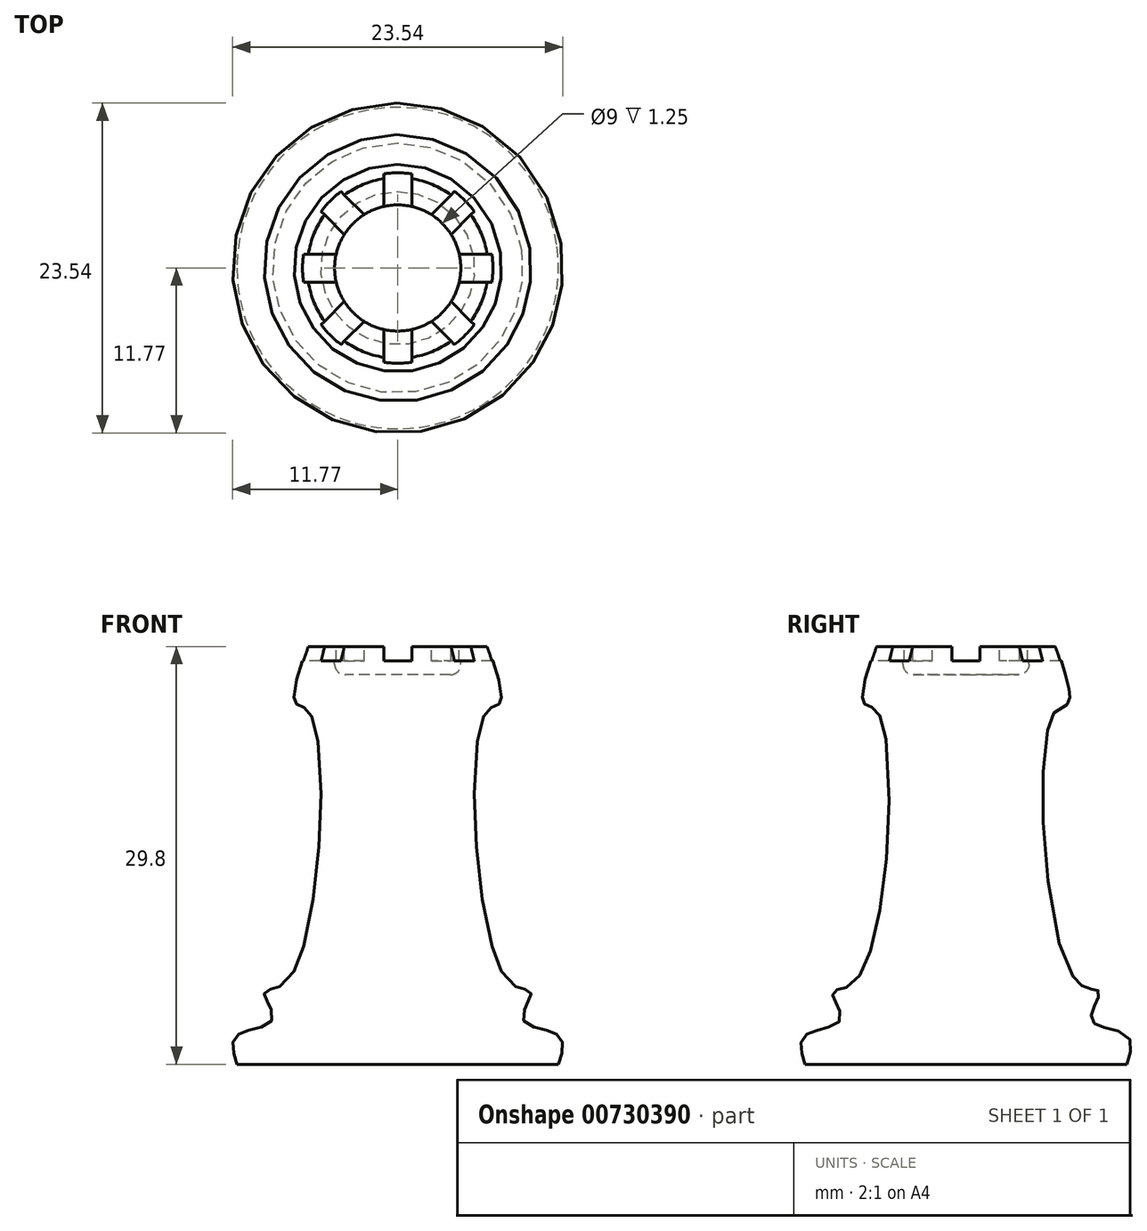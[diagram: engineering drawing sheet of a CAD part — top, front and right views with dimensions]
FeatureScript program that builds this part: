
annotation { "Feature Type Name" : "Feature", "Feature Type Description" : "" }
export const myFeature = defineFeature(function(context is Context, id is Id, definition is map)
    precondition{}
    {
        {
            var Q0;
            Q0=qCreatedBy(makeId("Front.planeOp"),FACE);
            var sketch = newSketch(context, id + "F0", { "sketchPlane" : qUnion([Q0])});
            skLineSegment(sketch, "E0", {"start": v(0, 0) * mm, "end": v(0, 29.8) * mm});
            skLineSegment(sketch, "E1", {"start": v(0, 0) * mm, "end": v(11.47, 0) * mm});
            skFitSpline(sketch, "E2", {"points": [v(11.47, 0) * mm, v(11.47, 2.06) * mm, v(8.96, 3.18) * mm, v(9.52, 5.13) * mm, v(7.84, 5.97) * mm, v(6.17, 24.93) * mm, v(7.29, 25.77) * mm, v(6.45, 29.8) * mm], "startDerivative": vector(7.38, 22.92) * mm, "endDerivative": vector(-11.94, 34.46) * mm});
            skLineSegment(sketch, "E3", {"start": v(6.45, 29.8) * mm, "end": v(0, 29.8) * mm});
            skSolve(sketch);
        }
        {
            var Q0;
            Q0=makeQuery(id+"F0.imprint","IMPRINT",FACE,{"disambiguationData":[TD([[makeQuery(id+"F0.imprint","IMPRINT",EDGE,{"derivedFrom":sQuery(id+"F0.wireOp",EDGE,"E0")}),-1.0]])]});
            var Q1;
            Q1=sQuery(id+"F0.wireOp",EDGE,"E0");
            revolve(context, id + "F1", {"surfaceOperationType" : NewSurfaceOperationType.NEW, "entities" : qUnion([Q0]), "axis" : qUnion([Q1]), "revolveType" : RevolveType.FULL});
        }
        {
            var Q0;
            Q0=makeQuery(id+"F1.opRevolve","SWEPT_FACE",FACE,{"disambiguationData":[OSD([sQuery(id+"F0.wireOp",EDGE,"E3")])]});
            var sketch = newSketch(context, id + "F2", { "sketchPlane" : qUnion([Q0])});
            skCircle(sketch, "E4", {"center": v(0, 0) * mm, "radius": 4.5 * mm});
            skSolve(sketch);
        }
        {
            var Q0;
            Q0=makeQuery(id+"F2.imprint","IMPRINT",FACE,{"disambiguationData":[TD([[makeQuery(id+"F2.imprint","IMPRINT",EDGE,{"derivedFrom":sQuery(id+"F2.wireOp",EDGE,"E4")}),1.0]])]});
            extrude(context, id + "F3", {"entities" : qUnion([Q0]), "operationType" : NewBodyOperationType.REMOVE, "oppositeDirection" : true, "depth" : 2 * mm, "offsetDistance" : 25 * mm});
        }
        {
            var Q0;
            Q0=makeQuery(id+"F1.opRevolve","SWEPT_FACE",FACE,{"disambiguationData":[OSD([sQuery(id+"F0.wireOp",EDGE,"E3")])]});
            var sketch = newSketch(context, id + "F4", { "sketchPlane" : qUnion([Q0])});
            skLineSegment(sketch, "E5.bottom", {"start": v(-1, 7.5) * mm, "end": v(1, 7.5) * mm});
            skLineSegment(sketch, "E5.top", {"start": v(-1, -7.5) * mm, "end": v(1, -7.5) * mm});
            skLineSegment(sketch, "E5.left", {"start": v(-1, 7.5) * mm, "end": v(-1, -7.5) * mm});
            skLineSegment(sketch, "E5.right", {"start": v(1, 7.5) * mm, "end": v(1, -7.5) * mm});
            skPoint(sketch, "E5.middle", {"position": v(0, 0) * mm});
            skLineSegment(sketch, "E6.1.0", {"start": v(6.01, 4.6) * mm, "end": v(-4.6, -6.01) * mm});
            skLineSegment(sketch, "E6.1.1", {"start": v(4.6, 6.01) * mm, "end": v(-6.01, -4.6) * mm});
            skLineSegment(sketch, "E6.1.2", {"start": v(4.6, 6.01) * mm, "end": v(6.01, 4.6) * mm});
            skLineSegment(sketch, "E6.1.3", {"start": v(-6.01, -4.6) * mm, "end": v(-4.6, -6.01) * mm});
            skLineSegment(sketch, "E6.2.0", {"start": v(7.5, -1) * mm, "end": v(-7.5, -1) * mm});
            skLineSegment(sketch, "E6.2.1", {"start": v(7.5, 1) * mm, "end": v(-7.5, 1) * mm});
            skLineSegment(sketch, "E6.2.2", {"start": v(7.5, 1) * mm, "end": v(7.5, -1) * mm});
            skLineSegment(sketch, "E6.2.3", {"start": v(-7.5, 1) * mm, "end": v(-7.5, -1) * mm});
            skLineSegment(sketch, "E6.3.0", {"start": v(4.6, -6.01) * mm, "end": v(-6.01, 4.6) * mm});
            skLineSegment(sketch, "E6.3.1", {"start": v(6.01, -4.6) * mm, "end": v(-4.6, 6.01) * mm});
            skLineSegment(sketch, "E6.3.2", {"start": v(6.01, -4.6) * mm, "end": v(4.6, -6.01) * mm});
            skLineSegment(sketch, "E6.3.3", {"start": v(-4.6, 6.01) * mm, "end": v(-6.01, 4.6) * mm});
            skLineSegment(sketch, "E6.4.0", {"start": v(-1, -7.5) * mm, "end": v(-1, 7.5) * mm});
            skLineSegment(sketch, "E6.4.1", {"start": v(1, -7.5) * mm, "end": v(1, 7.5) * mm});
            skLineSegment(sketch, "E6.4.2", {"start": v(1, -7.5) * mm, "end": v(-1, -7.5) * mm});
            skLineSegment(sketch, "E6.4.3", {"start": v(1, 7.5) * mm, "end": v(-1, 7.5) * mm});
            skLineSegment(sketch, "E6.anchor1", {"start": v(0, 0) * mm, "end": v(1, -7.5) * mm, "construction": true});
            skLineSegment(sketch, "E6.anchor2", {"start": v(0, 0) * mm, "end": v(-1, 7.5) * mm, "construction": true});
            skSolve(sketch);
        }
        {
            var Q0;
            Q0 = qSketchRegion(id + "F4", true);
            extrude(context, id + "F5", {"entities" : qUnion([Q0]), "operationType" : NewBodyOperationType.REMOVE, "oppositeDirection" : true, "depth" : 1 * mm, "offsetDistance" : 25 * mm});
        }
        {
            var Q0;
            Q0=makeQuery(id+"F3.boolean.opBoolean","COPY",EDGE,{"derivedFrom":makeQuery(id+"F3.opExtrude","CAP_EDGE",EDGE,{"disambiguationData":[OSD([sQuery(id+"F2.wireOp",EDGE,"E4")])],"isStart":false})});
            fillet(context, id + "F6", {"entities" : qUnion([Q0]), "radius" : .75 * mm, "tangentPropagation" : true, "allowEdgeOverflow" : false});
        }
    });
